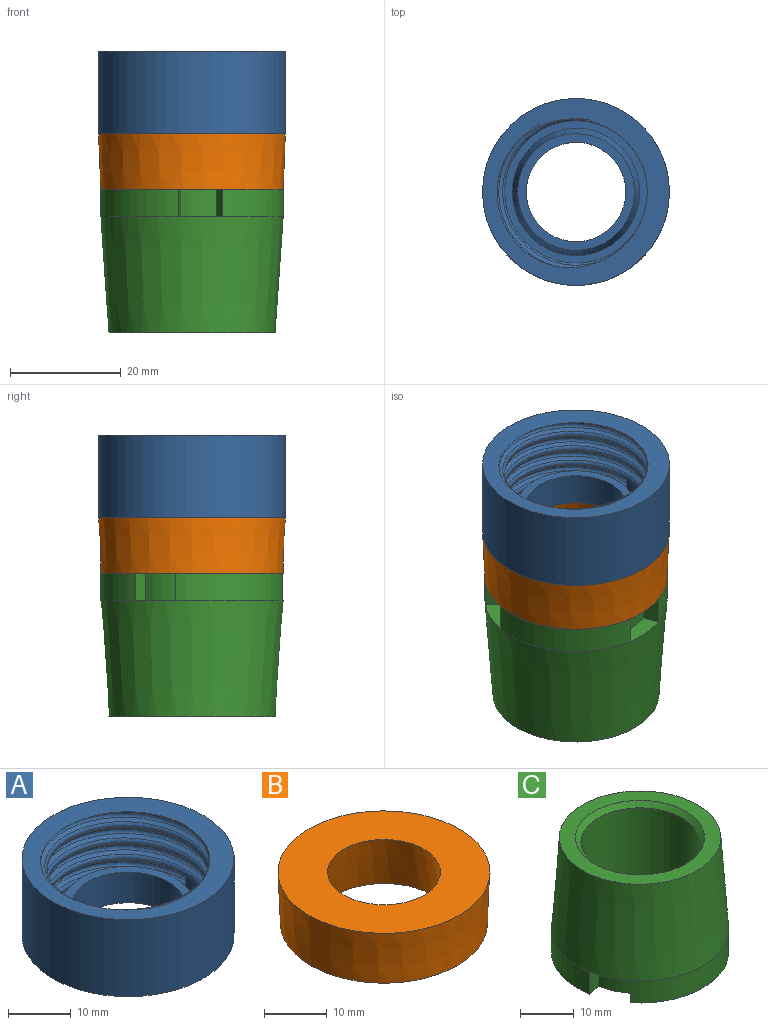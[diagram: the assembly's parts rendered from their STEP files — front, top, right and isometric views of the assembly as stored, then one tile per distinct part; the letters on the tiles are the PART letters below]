
ASSEMBLY  parts=3 mates=2
PART A: 15 faces, bbox 34.2x34.2x16.8 mm
  f0: cylinder r=12.9mm len=25.8mm, axis (0,0,1), area 148mm2, adj f1,f2,f6,f10,f11
  f1: plane 2.23x1.42mm, normal (0,1,0), area 1.8mm2, adj f0,f3,f7,f8,f9,f10,f11
  f2: bspline ~30.63x26.52mm, area 223.8mm2, adj f0,f3,f6,f11
  f3: bspline ~32.24x27.92mm, area 252.1mm2, adj f1,f2,f6,f7,f11
  f4: cylinder r=16.9mm len=33.8mm, axis (0,0,1), area 1592.8mm2, adj f5,f6
  f5: plane 33.8x33.8mm, normal (0,0,-1), area 642.8mm2, adj f4,f12
  f6: plane 34.13x34.13mm, normal (0,0,1), area 323.8mm2, adj f0,f2,f3,f4,f7,f8,f9,f10
  f7: bspline ~27.92x27.91mm, area 0.1mm2, adj f1,f3,f6,f8
  f8: bspline ~33.33x28.86mm, area 390.9mm2, adj f1,f6,f7,f9
  f9: bspline ~32.25x27.93mm, area 224.2mm2, adj f1,f6,f8,f10
  f10: bspline ~30.63x26.52mm, area 188.5mm2, adj f0,f1,f6,f9
  f11: plane 26.76x26.17mm, normal (0,0,1), area 108.5mm2, adj f0,f1,f2,f3,f13
  f12: cylinder r=9mm len=18mm, axis (0,0,-1), area 339.3mm2, adj f5,f14
  f13: cone r=12.5mm half-angle=18deg, axis (0,0,-1), area 218.8mm2, adj f11,f14
  f14: plane 21.1x21.1mm, normal (0,0,1), area 95.2mm2, adj f12,f13
PART B: 4 faces, bbox 33.8x33.8x10 mm
  f0: cone r=9mm half-angle=11.3deg, axis (0,0,-1), area 640.8mm2, adj f1,f3
  f1: plane 33.8x33.8mm, normal (0,0,1), area 642.8mm2, adj f0,f2
  f2: cone r=16.9mm half-angle=2.3deg, axis (0,0,1), area 1050.1mm2, adj f1,f3
  f3: plane 33x33mm, normal (0,0,-1), area 475.2mm2, adj f0,f2
PART C: 20 faces, bbox 33x33x26 mm
  f0: plane 7.96x3.77mm, normal (0,0,-1), area 22mm2, adj f2,f11,f12,f13
  f1: plane 7.82x5.67mm, normal (0,0,-1), area 22mm2, adj f2,f15,f16,f17
  f2: cone r=16.5mm half-angle=4deg, axis (0,0,-1), area 2085.3mm2, adj f0,f1,f4,f5,f14,f18,f19
  f3: cylinder r=11mm len=25mm, axis (0,0,-1), area 1727.9mm2, adj f6,f7
  f4: plane 30.06x30.06mm, normal (0,0,1), area 257.4mm2, adj f2,f6
  f5: plane 7.61x6.59mm, normal (0,0,-1), area 22mm2, adj f2,f8,f9,f10
  f6: cone r=11mm half-angle=45deg, axis (0,0,1), area 102.2mm2, adj f3,f4
  f7: plane 33x32.81mm, normal (0,0,-1), area 409.1mm2, adj f3,f8,f9,f10,f11,f12,f13,f14
  f8: cylinder r=13.5mm len=5.34mm, axis (0,0,1), area 33.1mm2, adj f5,f7,f9,f10
  f9: plane 5x2.28mm, normal (0.76,0.65,0), area 15mm2, adj f5,f7,f8,f19
  f10: plane 5x2.79mm, normal (-0.36,-0.93,0), area 15mm2, adj f5,f7,f8,f14
  f11: plane 5x2.97mm, normal (0.99,0.15,0), area 15mm2, adj f0,f7,f13,f18
  f12: plane 5x2.83mm, normal (-0.94,0.33,0), area 15mm2, adj f0,f7,f13,f14
  f13: cylinder r=13.5mm len=6.52mm, axis (0,0,1), area 33.1mm2, adj f0,f7,f11,f12
  f14: cylinder r=16.5mm len=21.57mm, axis (0,0,-1), area 132.4mm2, adj f2,f7,f10,f12
  f15: plane 5x2.34mm, normal (-0.62,0.78,0), area 15mm2, adj f1,f7,f17,f19
  f16: plane 5x2.95mm, normal (0.18,-0.98,0), area 15mm2, adj f1,f7,f17,f18
  f17: cylinder r=13.5mm len=5.95mm, axis (0,0,1), area 33.1mm2, adj f1,f7,f15,f16
  f18: cylinder r=16.5mm len=19.34mm, axis (0,0,-1), area 132.4mm2, adj f2,f7,f11,f16
  f19: cylinder r=16.5mm len=23.62mm, axis (0,0,-1), area 132.4mm2, adj f2,f7,f9,f15
PLACE A t=(2.21,15.67,-11.45)mm
PLACE B t=(2.21,15.67,14.35)mm
PLACE C rot(axis=(1,0,0),180deg) t=(2.21,15.67,9.35)mm
MATE fastened B.f0 <-> C.f3  axis (0,0,1) through (2.21,15.67,14.35)mm
MATE fastened B.f0 <-> A.f4  axis (0,0,1) through (2.21,15.67,24.35)mm
